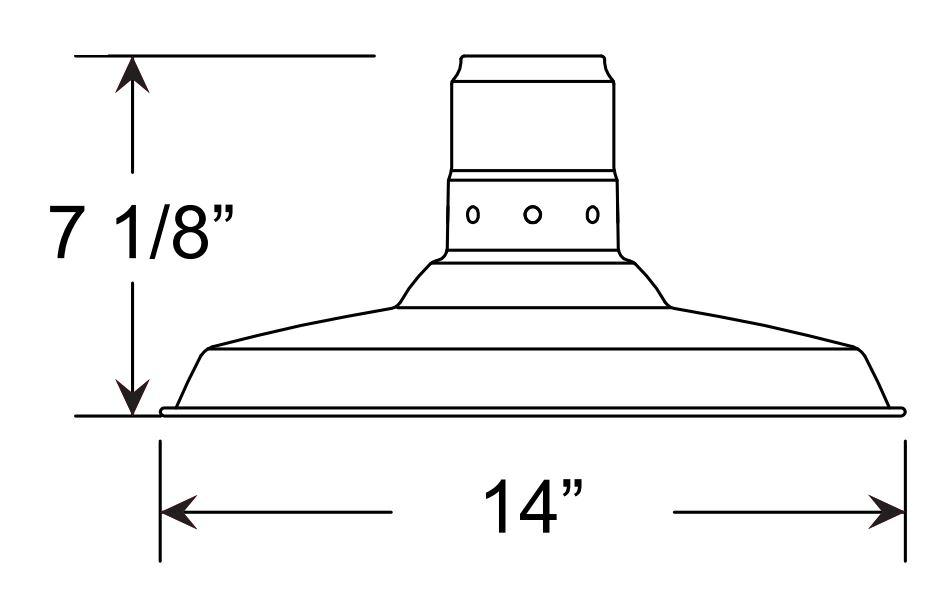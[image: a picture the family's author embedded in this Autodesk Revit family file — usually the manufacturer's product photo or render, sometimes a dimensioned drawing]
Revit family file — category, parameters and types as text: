
# Revit family: SPO-AB MB
name_source: partatom
category: Lighting Fixtures
units: mm (PartAtom-declared; Revit-internal decimal feet)

## family parameters
Always vertical = Yes
Cut with Voids When Loaded = No
Light Source = Yes
OmniClass Number = 23.80.70.00
OmniClass Title = Lighting
Part Type = Normal
Room Calculation Point = No
Round Connector Dimension = Use Diameter
Shared = No
Work Plane-Based = No

## types (1)
- SPO-AB
    Apparent Load = 60 VA
    Body Colour = Spun aluminium
    Body Material = body
    Color Filter = 16777215
    Construction Material = Heavy Duty spun aluminum.
    Default Elevation = 0' - 0"
    Description = 120-277 Voltage
    Dimming Lamp Color Temperature Shift = <None>
    Fixture Diameter = 0' - 1 1/2"
    Fixture Height = 0' - 2 1/2"
    GLASS = Glass
    Lamp = MED-BASE
    Load Classification = Lighting
    Manufacturer = ANP Lighting
    Model = SPO-AB
    Photometric Web File = generic.ies
    Power Factor = 1
    Ring = RING
    SPO-AB = Yes
    Tilt Angle = 90.00°
    URL = https://www.anplighting.com
    Voltage = 277 V
    Warranty = 5 year limited warranty
    Wattage Comments = 60W Max
    Weight = 0.30 lbs

## geometry (parser evidence)
native form markers: Sweep x23
no freeform markers — native parametric forms only
